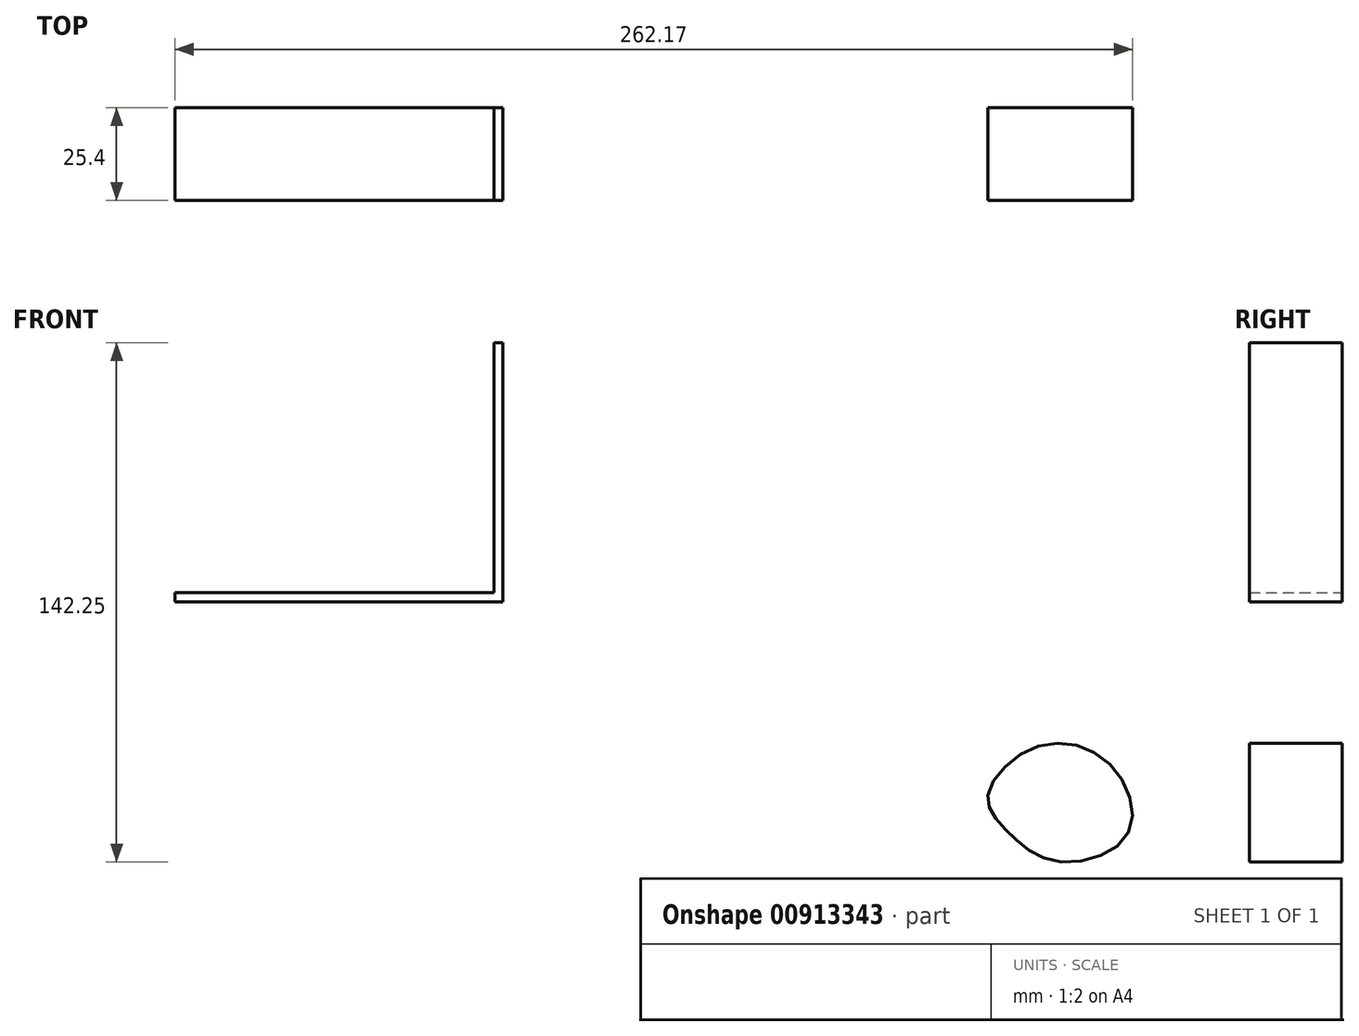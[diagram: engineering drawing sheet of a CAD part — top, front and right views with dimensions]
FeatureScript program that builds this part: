
annotation { "Feature Type Name" : "Feature", "Feature Type Description" : "" }
export const myFeature = defineFeature(function(context is Context, id is Id, definition is map)
    precondition{}
    {
        {
            var Q0;
            Q0=qCreatedBy(makeId("Front.planeOp"),FACE);
            var sketch = newSketch(context, id + "F0", { "sketchPlane" : qUnion([Q0])});
            skLineSegment(sketch, "E0", {"start": v(213.06, 34.17) * mm, "end": v(190.85, 34.17) * mm});
            skLineSegment(sketch, "E1", {"start": v(190.85, 34.17) * mm, "end": v(170.57, 6.65) * mm});
            skLineSegment(sketch, "E2", {"start": v(170.57, 6.65) * mm, "end": v(183.88, -3.16) * mm});
            skLineSegment(sketch, "E3", {"start": v(183.88, -3.16) * mm, "end": v(195.59, 12.74) * mm});
            skLineSegment(sketch, "E4", {"start": v(195.59, 12.74) * mm, "end": v(195.59, -36.82) * mm});
            skLineSegment(sketch, "E5", {"start": v(195.59, -36.82) * mm, "end": v(209.68, -36.82) * mm});
            skLineSegment(sketch, "E6", {"start": v(213.06, 39) * mm, "end": v(213.06, -44.06) * mm, "construction": true});
            skLineSegment(sketch, "E7.MirrorCS", {"start": v(230.53, 12.74) * mm, "end": v(230.53, -36.82) * mm});
            skLineSegment(sketch, "E8.MirrorCS", {"start": v(235.27, 34.17) * mm, "end": v(255.55, 6.65) * mm});
            skLineSegment(sketch, "E9.MirrorCS", {"start": v(255.55, 6.65) * mm, "end": v(242.24, -3.16) * mm});
            skLineSegment(sketch, "E10.MirrorCS", {"start": v(230.53, -36.82) * mm, "end": v(216.44, -36.82) * mm});
            skLineSegment(sketch, "E11.MirrorCS", {"start": v(242.24, -3.16) * mm, "end": v(230.53, 12.74) * mm});
            skLineSegment(sketch, "E12.bottom", {"start": v(-38.04, 29.83) * mm, "end": v(51.78, 29.83) * mm});
            skLineSegment(sketch, "E12.top", {"start": v(-38.04, -41.16) * mm, "end": v(51.78, -41.16) * mm});
            skLineSegment(sketch, "E12.left", {"start": v(-38.04, 29.83) * mm, "end": v(-38.04, -41.16) * mm});
            skLineSegment(sketch, "E12.right", {"start": v(51.78, 29.83) * mm, "end": v(51.78, -41.16) * mm});
            skFitSpline(sketch, "E13", {"points": [v(189.4, -103.46) * mm, v(184.57, -94.28) * mm, v(198.1, -80.76) * mm, v(218.37, -86.07) * mm, v(222.72, -104.9) * mm, v(202.92, -112.15) * mm, v(189.4, -103.46) * mm]});
            skFitSpline(sketch, "E14.0", {"points": [v(174.2, -118.3) * mm, v(174.07, -118.16) * mm, v(173.93, -118.02) * mm, v(173.74, -117.82) * mm, v(173.5, -117.56) * mm, v(173.18, -117.23) * mm, v(172.75, -116.77) * mm, v(172.16, -116.13) * mm, v(171.4, -115.27) * mm, v(170.58, -114.3) * mm, v(169.42, -112.85) * mm, v(167.86, -110.67) * mm, v(166.27, -107.86) * mm, v(165.12, -105.17) * mm, v(164.36, -102.94) * mm, v(163.76, -100.51) * mm, v(163.37, -97.92) * mm, v(163.25, -95.69) * mm, v(163.3, -93.88) * mm, v(163.37, -92.76) * mm, v(163.47, -91.86) * mm, v(163.58, -90.97) * mm, v(163.76, -89.9) * mm, v(164.02, -88.67) * mm, v(164.43, -87.1) * mm, v(165.02, -85.27) * mm, v(165.83, -83.26) * mm, v(166.72, -81.4) * mm, v(168, -79.08) * mm, v(169.73, -76.45) * mm, v(172, -73.6) * mm, v(174.47, -71) * mm, v(177.13, -68.6) * mm, v(180, -66.38) * mm, v(183.1, -64.35) * mm, v(185.92, -62.83) * mm, v(188.32, -61.75) * mm, v(189.9, -61.13) * mm, v(191.2, -60.67) * mm, v(192.52, -60.24) * mm, v(194.18, -59.77) * mm, v(196.2, -59.32) * mm, v(198.88, -58.87) * mm, v(202.24, -58.56) * mm, v(206.23, -58.6) * mm, v(211.45, -59.15) * mm, v(217.75, -60.76) * mm, v(223.6, -63.49) * mm, v(227.4, -65.95) * mm, v(229.47, -67.51) * mm, v(230.98, -68.76) * mm, v(232.2, -69.87) * mm, v(233.13, -70.78) * mm, v(234.05, -71.73) * mm, v(235.15, -72.94) * mm, v(236.8, -74.94) * mm, v(238.69, -77.56) * mm, v(240.64, -80.86) * mm, v(242.31, -84.35) * mm, v(243.67, -88.04) * mm, v(244.7, -91.96) * mm, v(245.32, -96.13) * mm, v(245.45, -100.57) * mm, v(245.05, -104.49) * mm, v(244.35, -107.72) * mm, v(243.6, -110.16) * mm, v(242.8, -112.2) * mm, v(242.04, -113.82) * mm, v(241.4, -115.02) * mm, v(240.72, -116.21) * mm, v(239.99, -117.34) * mm, v(239.23, -118.42) * mm, v(238.18, -119.78) * mm, v(236.8, -121.35) * mm, v(235.1, -123.03) * mm, v(233.36, -124.53) * mm, v(231.01, -126.32) * mm, v(228.04, -128.18) * mm, v(224.46, -129.94) * mm, v(220.87, -131.31) * mm, v(217.28, -132.36) * mm, v(213.67, -133.1) * mm, v(210.02, -133.55) * mm, v(206.93, -133.69) * mm, v(204.41, -133.64) * mm, v(202.5, -133.51) * mm, v(200.87, -133.33) * mm, v(199.56, -133.13) * mm, v(198.23, -132.9) * mm, v(196.6, -132.54) * mm, v(194.72, -132.02) * mm, v(192.9, -131.42) * mm, v(190.58, -130.52) * mm, v(187.88, -129.24) * mm, v(185, -127.56) * mm, v(182.45, -125.8) * mm, v(180.23, -124.06) * mm, v(178.63, -122.66) * mm, v(177.48, -121.59) * mm, v(176.68, -120.82) * mm, v(175.94, -120.09) * mm, v(175.37, -119.5) * mm, v(174.95, -119.07) * mm, v(174.64, -118.76) * mm, v(174.4, -118.5) * mm, v(174.2, -118.3) * mm, v(174.07, -118.16) * mm, v(173.93, -118.02) * mm, v(174.2, -118.3) * mm]});
            skSolve(sketch);
        }
        {
            var Q0;
            Q0 = qSketchRegion(id + "F0", true);
            extrude(context, id + "F1", {"entities" : qUnion([Q0]), "depth" : 25.4 * mm, "offsetDistance" : 25.4 * mm});
        }
        {
            var Q0;
            Q0=makeQuery(id+"F1.opExtrude","CAP_FACE",FACE,{"disambiguationData":[OSD([sQuery(id+"F0.wireOp",EDGE,"E12.bottom"),sQuery(id+"F0.wireOp",EDGE,"E12.top"),sQuery(id+"F0.wireOp",EDGE,"E12.left"),sQuery(id+"F0.wireOp",EDGE,"E12.right")])],"isStart":false});
            var Q1;
            Q1=makeQuery(id+"F1.opExtrude","SWEPT_FACE",FACE,{"disambiguationData":[OSD([sQuery(id+"F0.wireOp",EDGE,"E12.bottom")])]});
            var Q2;
            Q2=makeQuery(id+"F1.opExtrude","SWEPT_FACE",FACE,{"disambiguationData":[OSD([sQuery(id+"F0.wireOp",EDGE,"E12.left")])]});
            var Q3;
            Q3=makeQuery(id+"F1.opExtrude","CAP_FACE",FACE,{"disambiguationData":[OSD([sQuery(id+"F0.wireOp",EDGE,"E12.bottom"),sQuery(id+"F0.wireOp",EDGE,"E12.top"),sQuery(id+"F0.wireOp",EDGE,"E12.left"),sQuery(id+"F0.wireOp",EDGE,"E12.right")])],"isStart":true});
            shell(context, id + "F2", {"entities" : qUnion([Q0, Q1, Q2, Q3]), "thickness" : 2.54 * mm});
        }
    });
